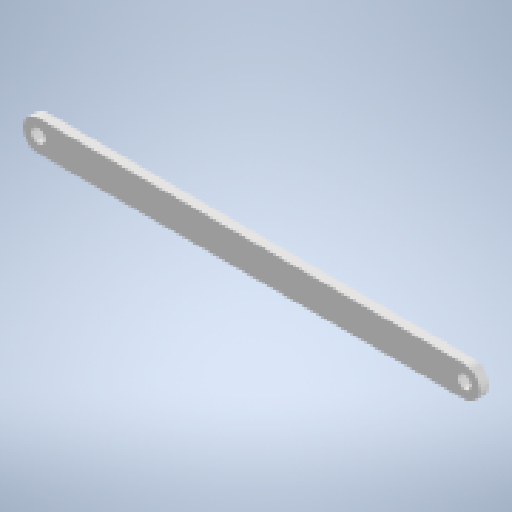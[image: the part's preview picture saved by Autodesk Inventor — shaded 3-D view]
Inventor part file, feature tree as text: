
AUTODESK INVENTOR PART (.ipt)
format: ipt  version: 2024.1 (Build 281209000, 209)  size: 140,288 bytes
history: native  units: mm
features: extrude x1, sketch x1
ambient origin geometry x8: Origin, YZ Plane, XZ Plane, XY Plane, X Axis, Y Axis, Z Axis, Center Point
bodies: Solid1 (feature_tree)
feature tree (2):
  extrude  "Extrusion1"  Depth=3.0mm
  sketch  "Sketch1"  dims[d0=135.404mm d1=4.25mm d2=3.0mm d3=0.0mm d4=0.5mm d5=0.872665mm]
